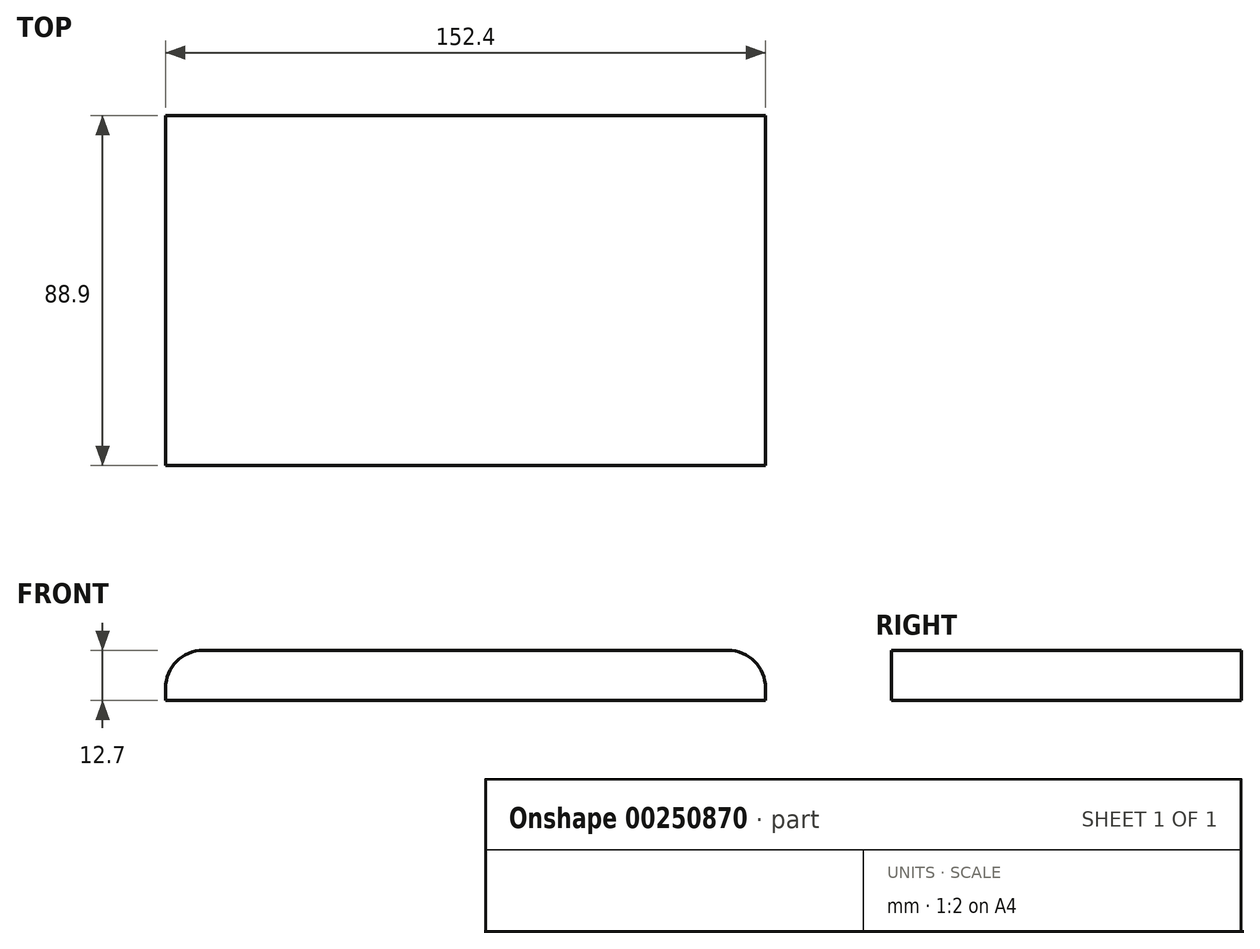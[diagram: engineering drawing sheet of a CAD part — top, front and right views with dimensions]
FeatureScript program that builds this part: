
annotation { "Feature Type Name" : "Feature", "Feature Type Description" : "" }
export const myFeature = defineFeature(function(context is Context, id is Id, definition is map)
    precondition{}
    {
        {
            var Q0;
            Q0=qCreatedBy(makeId("Top.planeOp"),FACE);
            var sketch = newSketch(context, id + "F0", { "sketchPlane" : qUnion([Q0])});
            skLineSegment(sketch, "E0.bottom", {"start": v(-84.5, 57.73) * mm, "end": v(67.9, 57.73) * mm});
            skLineSegment(sketch, "E0.top", {"start": v(-84.5, -31.17) * mm, "end": v(67.9, -31.17) * mm});
            skLineSegment(sketch, "E0.left", {"start": v(-84.5, 57.73) * mm, "end": v(-84.5, -31.17) * mm});
            skLineSegment(sketch, "E0.right", {"start": v(67.9, 57.73) * mm, "end": v(67.9, -31.17) * mm});
            skSolve(sketch);
        }
        {
            var Q0;
            Q0=qSketchRegion(id+"F0",true);
            extrude(context, id + "F1", {"entities" : qUnion([Q0]), "depth" : 12.7 * mm});
        }
        {
            var Q0;
            Q0=makeQuery(id+"F1.opExtrude","CAP_EDGE",EDGE,{"disambiguationData":[OSD([sQuery(id+"F0.wireOp",EDGE,"E0.right")])],"isStart":false});
            var Q1;
            Q1=makeQuery(id+"F1.opExtrude","CAP_EDGE",EDGE,{"disambiguationData":[OSD([sQuery(id+"F0.wireOp",EDGE,"E0.left")])],"isStart":false});
            fillet(context, id + "F2", {"entities" : qUnion([Q0, Q1]), "radius" : 9.52 * mm, "tangentPropagation" : true, "allowEdgeOverflow" : false});
        }
    });
